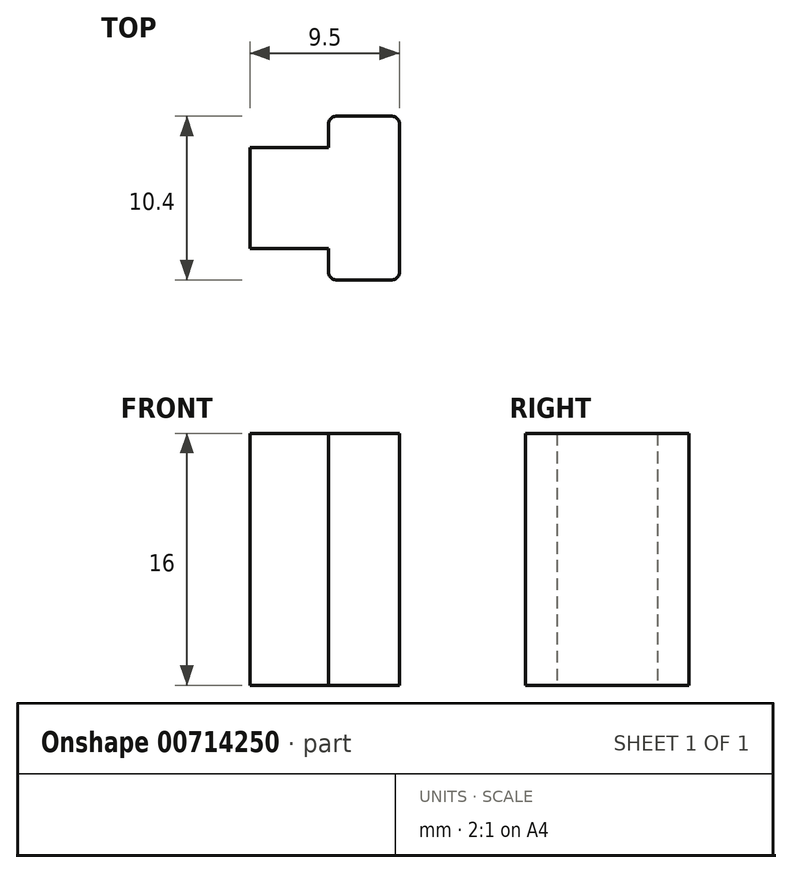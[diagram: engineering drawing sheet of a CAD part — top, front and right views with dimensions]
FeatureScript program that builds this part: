
annotation { "Feature Type Name" : "Feature", "Feature Type Description" : "" }
export const myFeature = defineFeature(function(context is Context, id is Id, definition is map)
    precondition{}
    {
        {
            var Q0;
            Q0=qCreatedBy(makeId("Top.planeOp"),FACE);
            var sketch = newSketch(context, id + "F0", { "sketchPlane" : qUnion([Q0])});
            skLineSegment(sketch, "E0", {"start": v(0, 0) * mm, "end": v(0, 4.7) * mm});
            skLineSegment(sketch, "E1", {"start": v(-0.5, 5.2) * mm, "end": v(-4, 5.2) * mm});
            skLineSegment(sketch, "E2", {"start": v(-4.5, 4.7) * mm, "end": v(-4.5, 3.2) * mm});
            skLineSegment(sketch, "E3", {"start": v(-4.5, 3.2) * mm, "end": v(-9.5, 3.2) * mm});
            skLineSegment(sketch, "E4", {"start": v(-9.5, 3.2) * mm, "end": v(-9.5, 0) * mm});
            skLineSegment(sketch, "E5.MirrorCS", {"start": v(-9.5, -3.2) * mm, "end": v(-9.5, 0) * mm});
            skLineSegment(sketch, "E6.MirrorCS", {"start": v(-4.5, -3.2) * mm, "end": v(-9.5, -3.2) * mm});
            skLineSegment(sketch, "E7.MirrorCS", {"start": v(-4.5, -4.7) * mm, "end": v(-4.5, -3.2) * mm});
            skLineSegment(sketch, "E8.MirrorCS", {"start": v(-0.5, -5.2) * mm, "end": v(-4, -5.2) * mm});
            skLineSegment(sketch, "E9.MirrorCS", {"start": v(0, 0) * mm, "end": v(0, -4.7) * mm});
            skPoint(sketch, "E10.visualSharp", {"position": v(0, -5.2) * mm});
            skArc(sketch, "E10.filletArc", {"start": v(-0.5, -5.2) * mm, "mid": v(-0.15, -5.05) * mm, "end": v(0, -4.7) * mm});
            skPoint(sketch, "E11.visualSharp", {"position": v(0, 5.2) * mm});
            skArc(sketch, "E11.filletArc", {"start": v(0, 4.7) * mm, "mid": v(-0.15, 5.05) * mm, "end": v(-0.5, 5.2) * mm});
            skPoint(sketch, "E12.visualSharp", {"position": v(-4.5, 5.2) * mm});
            skArc(sketch, "E12.filletArc", {"start": v(-4, 5.2) * mm, "mid": v(-4.35, 5.05) * mm, "end": v(-4.5, 4.7) * mm});
            skPoint(sketch, "E13.visualSharp", {"position": v(-4.5, -5.2) * mm});
            skArc(sketch, "E13.filletArc", {"start": v(-4.5, -4.7) * mm, "mid": v(-4.35, -5.05) * mm, "end": v(-4, -5.2) * mm});
            skSolve(sketch);
        }
        {
            var Q0;
            Q0=makeQuery(id+"F0.imprint","IMPRINT",FACE,{"disambiguationData":[TD([[makeQuery(id+"F0.imprint","IMPRINT",EDGE,{"derivedFrom":sQuery(id+"F0.wireOp",EDGE,"E0")}),1.0]])]});
            extrude(context, id + "F1", {"entities" : qUnion([Q0]), "depth" : 16 * mm, "offsetDistance" : 25 * mm});
        }
    });
